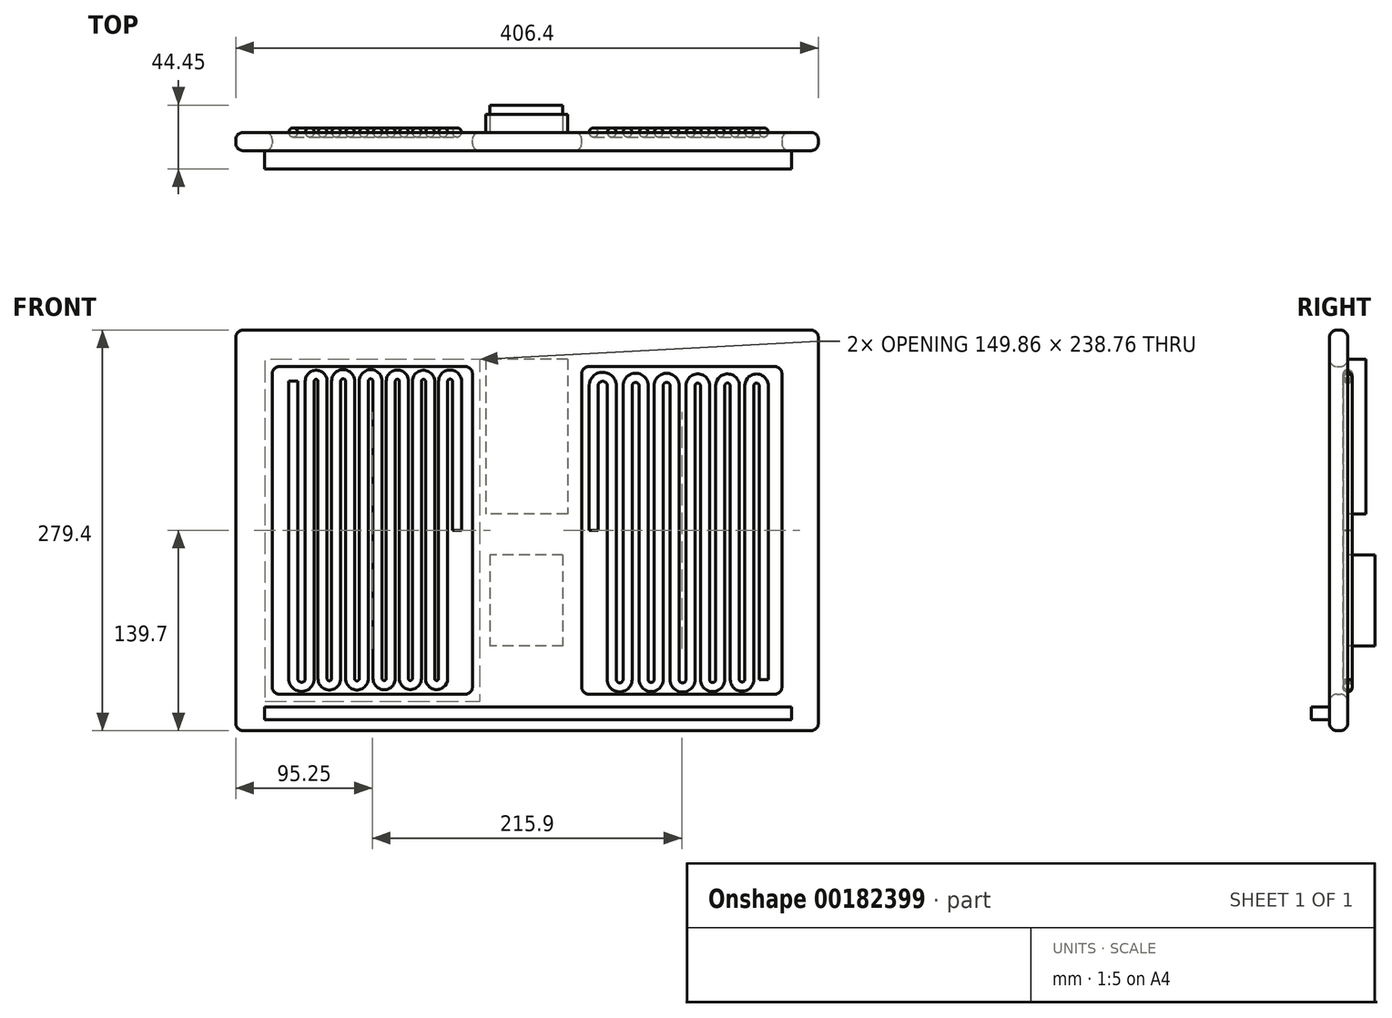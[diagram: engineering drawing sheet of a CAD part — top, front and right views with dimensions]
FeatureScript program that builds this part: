
annotation { "Feature Type Name" : "Feature", "Feature Type Description" : "" }
export const myFeature = defineFeature(function(context is Context, id is Id, definition is map)
    precondition{}
    {
        {
            var Q0;
            Q0=qCreatedBy(makeId("Front.planeOp"),FACE);
            var sketch = newSketch(context, id + "F0", { "sketchPlane" : qUnion([Q0])});
            skLineSegment(sketch, "E0.bottom", {"start": v(-203.2, 139.7) * mm, "end": v(203.2, 139.7) * mm});
            skLineSegment(sketch, "E0.top", {"start": v(-203.2, -139.7) * mm, "end": v(203.2, -139.7) * mm});
            skLineSegment(sketch, "E0.left", {"start": v(-203.2, 139.7) * mm, "end": v(-203.2, -139.7) * mm});
            skLineSegment(sketch, "E0.right", {"start": v(203.2, 139.7) * mm, "end": v(203.2, -139.7) * mm});
            skPoint(sketch, "E0.middle", {"position": v(0, 0) * mm});
            skSolve(sketch);
        }
        {
            var Q0;
            Q0=makeQuery(id+"F0.imprint","IMPRINT",FACE,{"disambiguationData":[TD([[makeQuery(id+"F0.imprint","IMPRINT",EDGE,{"derivedFrom":sQuery(id+"F0.wireOp",EDGE,"E0.bottom")}),-1.0]])]});
            extrude(context, id + "F1", {"entities" : qUnion([Q0]), "depth" : 12.7 * mm});
        }
        {
            var Q0;
            Q0=makeQuery(id+"F1.opExtrude","CAP_FACE",FACE,{"disambiguationData":[OSD([sQuery(id+"F0.wireOp",EDGE,"E0.bottom"),sQuery(id+"F0.wireOp",EDGE,"E0.top"),sQuery(id+"F0.wireOp",EDGE,"E0.left"),sQuery(id+"F0.wireOp",EDGE,"E0.right")])],"isStart":false});
            var sketch = newSketch(context, id + "F2", { "sketchPlane" : qUnion([Q0])});
            skLineSegment(sketch, "E1.bottom", {"start": v(-177.8, 114.3) * mm, "end": v(177.8, 114.3) * mm});
            skLineSegment(sketch, "E1.top", {"start": v(-177.8, -114.3) * mm, "end": v(177.8, -114.3) * mm});
            skLineSegment(sketch, "E1.left", {"start": v(-177.8, 114.3) * mm, "end": v(-177.8, -114.3) * mm});
            skLineSegment(sketch, "E1.right", {"start": v(177.8, 114.3) * mm, "end": v(177.8, -114.3) * mm});
            skPoint(sketch, "E1.middle", {"position": v(0, 0) * mm});
            skSolve(sketch);
        }
        {
            var Q0;
            Q0=makeQuery(id+"F2.imprint","IMPRINT",FACE,{"disambiguationData":[TD([[makeQuery(id+"F2.imprint","IMPRINT",EDGE,{"derivedFrom":sQuery(id+"F2.wireOp",EDGE,"E1.bottom")}),-1.0]])]});
            extrude(context, id + "F3", {"entities" : qUnion([Q0]), "operationType" : NewBodyOperationType.REMOVE, "oppositeDirection" : true, "depth" : 12.7 * mm});
        }
        {
            var Q0;
            Q0=qCreatedBy(makeId("Front.planeOp"),FACE);
            var sketch = newSketch(context, id + "F4", { "sketchPlane" : qUnion([Q0])});
            skLineSegment(sketch, "E2.bottom", {"start": v(-38.1, 114.3) * mm, "end": v(38.1, 114.3) * mm});
            skLineSegment(sketch, "E2.top", {"start": v(-38.1, -114.3) * mm, "end": v(38.1, -114.3) * mm});
            skLineSegment(sketch, "E2.left", {"start": v(-38.1, 114.3) * mm, "end": v(-38.1, -114.3) * mm});
            skLineSegment(sketch, "E2.right", {"start": v(38.1, 114.3) * mm, "end": v(38.1, -114.3) * mm});
            skPoint(sketch, "E2.middle", {"position": v(0, 0) * mm});
            skSolve(sketch);
        }
        {
            var Q0;
            Q0=makeQuery(id+"F4.imprint","IMPRINT",FACE,{"disambiguationData":[TD([[makeQuery(id+"F4.imprint","IMPRINT",EDGE,{"derivedFrom":sQuery(id+"F4.wireOp",EDGE,"E2.bottom")}),-1.0]])]});
            extrude(context, id + "F5", {"entities" : qUnion([Q0]), "operationType" : NewBodyOperationType.ADD, "depth" : 12.7 * mm});
        }
        {
            var Q0;
            Q0=makeQuery(id+"F1.opExtrude","SWEPT_FACE",FACE,{"disambiguationData":[OSD([sQuery(id+"F0.wireOp",EDGE,"E0.bottom")])]});
            var Q1;
            Q1=makeQuery(id+"F1.opExtrude","SWEPT_FACE",FACE,{"disambiguationData":[OSD([sQuery(id+"F0.wireOp",EDGE,"E0.top")])]});
            var Q2;
            Q2=makeQuery(id+"F1.opExtrude","SWEPT_FACE",FACE,{"disambiguationData":[OSD([sQuery(id+"F0.wireOp",EDGE,"E0.left")])]});
            var Q3;
            Q3=makeQuery(id+"F1.opExtrude","CAP_EDGE",EDGE,{"disambiguationData":[OSD([sQuery(id+"F0.wireOp",EDGE,"E0.bottom")])],"isStart":false});
            var Q4;
            Q4=makeQuery(id+"F1.opExtrude","SWEPT_FACE",FACE,{"disambiguationData":[OSD([sQuery(id+"F0.wireOp",EDGE,"E0.right")])]});
            var Q5;
            Q5=makeQuery(id+"F1.opExtrude","CAP_EDGE",EDGE,{"disambiguationData":[OSD([sQuery(id+"F0.wireOp",EDGE,"E0.top")])],"isStart":true});
            var Q6;
            Q6=makeQuery(id+"F1.opExtrude","CAP_EDGE",EDGE,{"disambiguationData":[OSD([sQuery(id+"F0.wireOp",EDGE,"E0.top")])],"isStart":false});
            var Q7;
            Q7=makeQuery(id+"F1.opExtrude","CAP_EDGE",EDGE,{"disambiguationData":[OSD([sQuery(id+"F0.wireOp",EDGE,"E0.left")])],"isStart":false});
            var Q8;
            Q8=makeQuery(id+"F1.opExtrude","CAP_EDGE",EDGE,{"disambiguationData":[OSD([sQuery(id+"F0.wireOp",EDGE,"E0.right")])],"isStart":true});
            var Q9;
            Q9=makeQuery(id+"F1.opExtrude","CAP_EDGE",EDGE,{"disambiguationData":[OSD([sQuery(id+"F0.wireOp",EDGE,"E0.right")])],"isStart":false});
            var Q10;
            Q10=makeQuery(id+"F3.boolean.opBoolean","COPY",FACE,{"derivedFrom":makeQuery(id+"F3.opExtrude","SWEPT_FACE",FACE,{"disambiguationData":[OSD([sQuery(id+"F2.wireOp",EDGE,"E1.left")])]})});
            var Q11;
            Q11=makeQuery(id+"F3.boolean.opBoolean","COPY",FACE,{"derivedFrom":makeQuery(id+"F3.opExtrude","SWEPT_FACE",FACE,{"disambiguationData":[OSD([sQuery(id+"F2.wireOp",EDGE,"E1.right")])]})});
            var Q12;
            Q12=makeQuery(id+"F3.boolean.opBoolean","COPY",EDGE,{"derivedFrom":makeQuery(id+"F3.opExtrude","CAP_EDGE",EDGE,{"disambiguationData":[OSD([sQuery(id+"F2.wireOp",EDGE,"E1.left")])],"isStart":true})});
            var Q13;
            Q13=makeQuery(id+"F3.boolean.opBoolean","COPY",EDGE,{"derivedFrom":makeQuery(id+"F3.opExtrude","CAP_EDGE",EDGE,{"disambiguationData":[OSD([sQuery(id+"F2.wireOp",EDGE,"E1.left")])],"isStart":false})});
            var Q14;
            Q14=makeQuery(id+"F3.boolean.opBoolean","COPY",EDGE,{"derivedFrom":makeQuery(id+"F3.opExtrude","CAP_EDGE",EDGE,{"disambiguationData":[OSD([sQuery(id+"F2.wireOp",EDGE,"E1.right")])],"isStart":true})});
            var Q15;
            Q15=makeQuery(id+"F5.opExtrude","SWEPT_FACE",FACE,{"disambiguationData":[OSD([sQuery(id+"F4.wireOp",EDGE,"E2.left")])]});
            var Q16;
            Q16=makeQuery(id+"F5.opExtrude","SWEPT_FACE",FACE,{"disambiguationData":[OSD([sQuery(id+"F4.wireOp",EDGE,"E2.right")])]});
            var Q17;
            Q17=makeQuery(id+"F5.opExtrude","CAP_EDGE",EDGE,{"disambiguationData":[OSD([sQuery(id+"F4.wireOp",EDGE,"E2.left")])],"isStart":false});
            var Q18;
            Q18=makeQuery(id+"F5.opExtrude","CAP_EDGE",EDGE,{"disambiguationData":[OSD([sQuery(id+"F4.wireOp",EDGE,"E2.right")])],"isStart":true});
            var Q19;
            Q19=makeQuery(id+"F5.opExtrude","CAP_EDGE",EDGE,{"disambiguationData":[OSD([sQuery(id+"F4.wireOp",EDGE,"E2.right")])],"isStart":false});
            var Q20;
            Q20=makeQuery(id+"F5.boolean.opBoolean","MERGE",FACE,{"derivedFrom":[makeQuery(id+"F1.opExtrude","CAP_FACE",FACE,{"disambiguationData":[OSD([sQuery(id+"F0.wireOp",EDGE,"E0.bottom"),sQuery(id+"F0.wireOp",EDGE,"E0.top"),sQuery(id+"F0.wireOp",EDGE,"E0.left"),sQuery(id+"F0.wireOp",EDGE,"E0.right")])],"isStart":true}),makeQuery(id+"F5.opExtrude","CAP_FACE",FACE,{"disambiguationData":[OSD([sQuery(id+"F4.wireOp",EDGE,"E2.bottom"),sQuery(id+"F4.wireOp",EDGE,"E2.top"),sQuery(id+"F4.wireOp",EDGE,"E2.left"),sQuery(id+"F4.wireOp",EDGE,"E2.right")])],"isStart":true})]});
            var Q21;
            Q21=makeQuery(id+"F5.boolean.opBoolean","MERGE",FACE,{"derivedFrom":[makeQuery(id+"F1.opExtrude","CAP_FACE",FACE,{"disambiguationData":[OSD([sQuery(id+"F0.wireOp",EDGE,"E0.bottom"),sQuery(id+"F0.wireOp",EDGE,"E0.top"),sQuery(id+"F0.wireOp",EDGE,"E0.left"),sQuery(id+"F0.wireOp",EDGE,"E0.right")])],"isStart":false}),makeQuery(id+"F5.opExtrude","CAP_FACE",FACE,{"disambiguationData":[OSD([sQuery(id+"F4.wireOp",EDGE,"E2.bottom"),sQuery(id+"F4.wireOp",EDGE,"E2.top"),sQuery(id+"F4.wireOp",EDGE,"E2.left"),sQuery(id+"F4.wireOp",EDGE,"E2.right")])],"isStart":false})]});
            var Q22;
            Q22=makeQuery(id+"F5.boolean.opBoolean","SPLIT",FACE,{"disambiguationData":[TD([makeQuery(id+"F3.boolean.opBoolean","COPY",FACE,{"derivedFrom":makeQuery(id+"F3.opExtrude","SWEPT_FACE",FACE,{"disambiguationData":[OSD([sQuery(id+"F2.wireOp",EDGE,"E1.left")])]})})])],"derivedFrom":makeQuery(id+"F3.boolean.opBoolean","COPY",FACE,{"derivedFrom":makeQuery(id+"F3.opExtrude","SWEPT_FACE",FACE,{"disambiguationData":[OSD([sQuery(id+"F2.wireOp",EDGE,"E1.bottom")])]})})});
            var Q23;
            Q23=makeQuery(id+"F5.boolean.opBoolean","SPLIT",FACE,{"disambiguationData":[TD([makeQuery(id+"F3.boolean.opBoolean","COPY",FACE,{"derivedFrom":makeQuery(id+"F3.opExtrude","SWEPT_FACE",FACE,{"disambiguationData":[OSD([sQuery(id+"F2.wireOp",EDGE,"E1.right")])]})})])],"derivedFrom":makeQuery(id+"F3.boolean.opBoolean","COPY",FACE,{"derivedFrom":makeQuery(id+"F3.opExtrude","SWEPT_FACE",FACE,{"disambiguationData":[OSD([sQuery(id+"F2.wireOp",EDGE,"E1.bottom")])]})})});
            var Q24;
            {var subQ0=sQuery(id+"F2.wireOp",EDGE,"E1.bottom");Q24=makeQuery(id+"F5.boolean.opBoolean","SPLIT",EDGE,{"disambiguationData":[TD([makeQuery(id+"F3.boolean.opBoolean","COPY",FACE,{"derivedFrom":makeQuery(id+"F3.opExtrude","SWEPT_FACE",FACE,{"disambiguationData":[OSD([sQuery(id+"F2.wireOp",EDGE,"E1.left")])]})})])],"derivedFrom":makeQuery(id+"F3.boolean.opBoolean","COPY",EDGE,{"derivedFrom":makeQuery(id+"F3.opExtrude","CAP_EDGE",EDGE,{"disambiguationData":[OSD([subQ0])],"isStart":true})})});}
            var Q25;
            {var subQ1=sQuery(id+"F2.wireOp",EDGE,"E1.bottom");Q25=makeQuery(id+"F5.boolean.opBoolean","SPLIT",EDGE,{"disambiguationData":[TD([makeQuery(id+"F3.boolean.opBoolean","COPY",FACE,{"derivedFrom":makeQuery(id+"F3.opExtrude","SWEPT_FACE",FACE,{"disambiguationData":[OSD([sQuery(id+"F2.wireOp",EDGE,"E1.left")])]})})])],"derivedFrom":makeQuery(id+"F3.boolean.opBoolean","COPY",EDGE,{"derivedFrom":makeQuery(id+"F3.opExtrude","CAP_EDGE",EDGE,{"disambiguationData":[OSD([subQ1])],"isStart":false})})});}
            var Q26;
            {var subQ1=sQuery(id+"F2.wireOp",EDGE,"E1.bottom");Q26=makeQuery(id+"F5.boolean.opBoolean","SPLIT",EDGE,{"disambiguationData":[TD([makeQuery(id+"F3.boolean.opBoolean","COPY",FACE,{"derivedFrom":makeQuery(id+"F3.opExtrude","SWEPT_FACE",FACE,{"disambiguationData":[OSD([sQuery(id+"F2.wireOp",EDGE,"E1.right")])]})})])],"derivedFrom":makeQuery(id+"F3.boolean.opBoolean","COPY",EDGE,{"derivedFrom":makeQuery(id+"F3.opExtrude","CAP_EDGE",EDGE,{"disambiguationData":[OSD([subQ1])],"isStart":false})})});}
            var Q27;
            {var subQ0=sQuery(id+"F2.wireOp",EDGE,"E1.top");Q27=makeQuery(id+"F5.boolean.opBoolean","SPLIT",EDGE,{"disambiguationData":[TD([makeQuery(id+"F3.boolean.opBoolean","COPY",FACE,{"derivedFrom":makeQuery(id+"F3.opExtrude","SWEPT_FACE",FACE,{"disambiguationData":[OSD([sQuery(id+"F2.wireOp",EDGE,"E1.left")])]})})])],"derivedFrom":makeQuery(id+"F3.boolean.opBoolean","COPY",EDGE,{"derivedFrom":makeQuery(id+"F3.opExtrude","CAP_EDGE",EDGE,{"disambiguationData":[OSD([subQ0])],"isStart":true})})});}
            var Q28;
            Q28=makeQuery(id+"F1.opExtrude","SWEPT_EDGE",EDGE,{"disambiguationData":[OSD([sQuery(id+"F0.wireOp",EDGE,"E0.bottom"),sQuery(id+"F0.wireOp",EDGE,"E0.left")])]});
            var Q29;
            Q29=makeQuery(id+"F1.opExtrude","SWEPT_EDGE",EDGE,{"disambiguationData":[OSD([sQuery(id+"F0.wireOp",EDGE,"E0.bottom"),sQuery(id+"F0.wireOp",EDGE,"E0.right")])]});
            var Q30;
            Q30=makeQuery(id+"F1.opExtrude","SWEPT_EDGE",EDGE,{"disambiguationData":[OSD([sQuery(id+"F0.wireOp",EDGE,"E0.top"),sQuery(id+"F0.wireOp",EDGE,"E0.left")])]});
            var Q31;
            Q31=makeQuery(id+"F1.opExtrude","SWEPT_EDGE",EDGE,{"disambiguationData":[OSD([sQuery(id+"F0.wireOp",EDGE,"E0.top"),sQuery(id+"F0.wireOp",EDGE,"E0.right")])]});
            var Q32;
            Q32=makeQuery(id+"F1.opExtrude","CAP_EDGE",EDGE,{"disambiguationData":[OSD([sQuery(id+"F0.wireOp",EDGE,"E0.bottom")])],"isStart":true});
            var Q33;
            Q33=makeQuery(id+"F1.opExtrude","CAP_EDGE",EDGE,{"disambiguationData":[OSD([sQuery(id+"F0.wireOp",EDGE,"E0.left")])],"isStart":true});
            var Q34;
            Q34=makeQuery(id+"F3.boolean.opBoolean","COPY",EDGE,{"derivedFrom":makeQuery(id+"F3.opExtrude","SWEPT_EDGE",EDGE,{"disambiguationData":[OSD([sQuery(id+"F2.wireOp",EDGE,"E1.bottom"),sQuery(id+"F2.wireOp",EDGE,"E1.left")])]})});
            var Q35;
            Q35=makeQuery(id+"F3.boolean.opBoolean","COPY",EDGE,{"derivedFrom":makeQuery(id+"F3.opExtrude","SWEPT_EDGE",EDGE,{"disambiguationData":[OSD([sQuery(id+"F2.wireOp",EDGE,"E1.bottom"),sQuery(id+"F2.wireOp",EDGE,"E1.right")])]})});
            var Q36;
            Q36=makeQuery(id+"F3.boolean.opBoolean","COPY",EDGE,{"derivedFrom":makeQuery(id+"F3.opExtrude","CAP_EDGE",EDGE,{"disambiguationData":[OSD([sQuery(id+"F2.wireOp",EDGE,"E1.right")])],"isStart":false})});
            var Q37;
            Q37=makeQuery(id+"F5.opExtrude","CAP_EDGE",EDGE,{"disambiguationData":[OSD([sQuery(id+"F4.wireOp",EDGE,"E2.left")])],"isStart":true});
            var Q38;
            Q38=makeQuery(id+"F5.opExtrude","SWEPT_EDGE",EDGE,{"disambiguationData":[OSD([sQuery(id+"F4.wireOp",EDGE,"E2.bottom"),sQuery(id+"F4.wireOp",EDGE,"E2.left")])]});
            var Q39;
            Q39=makeQuery(id+"F5.opExtrude","SWEPT_EDGE",EDGE,{"disambiguationData":[OSD([sQuery(id+"F4.wireOp",EDGE,"E2.bottom"),sQuery(id+"F4.wireOp",EDGE,"E2.right")])]});
            var Q40;
            Q40=makeQuery(id+"F5.opExtrude","SWEPT_EDGE",EDGE,{"disambiguationData":[OSD([sQuery(id+"F4.wireOp",EDGE,"E2.top"),sQuery(id+"F4.wireOp",EDGE,"E2.left")])]});
            var Q41;
            Q41=makeQuery(id+"F5.opExtrude","SWEPT_EDGE",EDGE,{"disambiguationData":[OSD([sQuery(id+"F4.wireOp",EDGE,"E2.top"),sQuery(id+"F4.wireOp",EDGE,"E2.right")])]});
            var Q42;
            Q42=makeQuery(id+"F5.boolean.opBoolean","SPLIT",FACE,{"disambiguationData":[TD([makeQuery(id+"F3.boolean.opBoolean","COPY",FACE,{"derivedFrom":makeQuery(id+"F3.opExtrude","SWEPT_FACE",FACE,{"disambiguationData":[OSD([sQuery(id+"F2.wireOp",EDGE,"E1.left")])]})})])],"derivedFrom":makeQuery(id+"F3.boolean.opBoolean","COPY",FACE,{"derivedFrom":makeQuery(id+"F3.opExtrude","SWEPT_FACE",FACE,{"disambiguationData":[OSD([sQuery(id+"F2.wireOp",EDGE,"E1.top")])]})})});
            var Q43;
            {var subQ0=sQuery(id+"F2.wireOp",EDGE,"E1.bottom");Q43=makeQuery(id+"F5.boolean.opBoolean","SPLIT",EDGE,{"disambiguationData":[TD([makeQuery(id+"F3.boolean.opBoolean","COPY",FACE,{"derivedFrom":makeQuery(id+"F3.opExtrude","SWEPT_FACE",FACE,{"disambiguationData":[OSD([sQuery(id+"F2.wireOp",EDGE,"E1.right")])]})})])],"derivedFrom":makeQuery(id+"F3.boolean.opBoolean","COPY",EDGE,{"derivedFrom":makeQuery(id+"F3.opExtrude","CAP_EDGE",EDGE,{"disambiguationData":[OSD([subQ0])],"isStart":true})})});}
            var Q44;
            Q44=makeQuery(id+"F5.boolean.opBoolean","SPLIT",FACE,{"disambiguationData":[TD([makeQuery(id+"F3.boolean.opBoolean","COPY",FACE,{"derivedFrom":makeQuery(id+"F3.opExtrude","SWEPT_FACE",FACE,{"disambiguationData":[OSD([sQuery(id+"F2.wireOp",EDGE,"E1.right")])]})})])],"derivedFrom":makeQuery(id+"F3.boolean.opBoolean","COPY",FACE,{"derivedFrom":makeQuery(id+"F3.opExtrude","SWEPT_FACE",FACE,{"disambiguationData":[OSD([sQuery(id+"F2.wireOp",EDGE,"E1.top")])]})})});
            var Q45;
            {var subQ0=sQuery(id+"F2.wireOp",EDGE,"E1.top");Q45=makeQuery(id+"F5.boolean.opBoolean","SPLIT",EDGE,{"disambiguationData":[TD([makeQuery(id+"F3.boolean.opBoolean","COPY",FACE,{"derivedFrom":makeQuery(id+"F3.opExtrude","SWEPT_FACE",FACE,{"disambiguationData":[OSD([sQuery(id+"F2.wireOp",EDGE,"E1.right")])]})})])],"derivedFrom":makeQuery(id+"F3.boolean.opBoolean","COPY",EDGE,{"derivedFrom":makeQuery(id+"F3.opExtrude","CAP_EDGE",EDGE,{"disambiguationData":[OSD([subQ0])],"isStart":true})})});}
            var Q46;
            {var subQ1=sQuery(id+"F2.wireOp",EDGE,"E1.top");Q46=makeQuery(id+"F5.boolean.opBoolean","SPLIT",EDGE,{"disambiguationData":[TD([makeQuery(id+"F3.boolean.opBoolean","COPY",FACE,{"derivedFrom":makeQuery(id+"F3.opExtrude","SWEPT_FACE",FACE,{"disambiguationData":[OSD([sQuery(id+"F2.wireOp",EDGE,"E1.right")])]})})])],"derivedFrom":makeQuery(id+"F3.boolean.opBoolean","COPY",EDGE,{"derivedFrom":makeQuery(id+"F3.opExtrude","CAP_EDGE",EDGE,{"disambiguationData":[OSD([subQ1])],"isStart":false})})});}
            var Q47;
            Q47=makeQuery(id+"F3.boolean.opBoolean","COPY",EDGE,{"derivedFrom":makeQuery(id+"F3.opExtrude","SWEPT_EDGE",EDGE,{"disambiguationData":[OSD([sQuery(id+"F2.wireOp",EDGE,"E1.top"),sQuery(id+"F2.wireOp",EDGE,"E1.left")])]})});
            var Q48;
            Q48=makeQuery(id+"F3.boolean.opBoolean","COPY",EDGE,{"derivedFrom":makeQuery(id+"F3.opExtrude","SWEPT_EDGE",EDGE,{"disambiguationData":[OSD([sQuery(id+"F2.wireOp",EDGE,"E1.top"),sQuery(id+"F2.wireOp",EDGE,"E1.right")])]})});
            var Q49;
            {var subQ1=sQuery(id+"F2.wireOp",EDGE,"E1.top");Q49=makeQuery(id+"F5.boolean.opBoolean","SPLIT",EDGE,{"disambiguationData":[TD([makeQuery(id+"F3.boolean.opBoolean","COPY",FACE,{"derivedFrom":makeQuery(id+"F3.opExtrude","SWEPT_FACE",FACE,{"disambiguationData":[OSD([sQuery(id+"F2.wireOp",EDGE,"E1.left")])]})})])],"derivedFrom":makeQuery(id+"F3.boolean.opBoolean","COPY",EDGE,{"derivedFrom":makeQuery(id+"F3.opExtrude","CAP_EDGE",EDGE,{"disambiguationData":[OSD([subQ1])],"isStart":false})})});}
            fillet(context, id + "F6", {"entities" : qUnion([Q0, Q1, Q2, Q3, Q4, Q5, Q6, Q7, Q8, Q9, Q10, Q11, Q12, Q13, Q14, Q15, Q16, Q17, Q18, Q19, Q20, Q21, Q22, Q23, Q24, Q25, Q26, Q27, Q28, Q29, Q30, Q31, Q32, Q33, Q34, Q35, Q36, Q37, Q38, Q39, Q40, Q41, Q42, Q43, Q44, Q45, Q46, Q47, Q48, Q49]), "radius" : 5.08 * mm, "tangentPropagation" : true, "allowEdgeOverflow" : false});
        }
        {
            var Q0;
            Q0=qCreatedBy(makeId("Front.planeOp"),FACE);
            var sketch = newSketch(context, id + "F7", { "sketchPlane" : qUnion([Q0])});
            skLineSegment(sketch, "E3", {"start": v(46.45, 0) * mm, "end": v(46.45, 100.84) * mm});
            skArc(sketch, "E4", {"start": v(46.45, 100.84) * mm, "mid": v(52.76, 107.15) * mm, "end": v(59.07, 100.84) * mm});
            skLineSegment(sketch, "E5", {"start": v(59.07, 100.84) * mm, "end": v(59.07, -104.04) * mm});
            skArc(sketch, "E6", {"start": v(59.07, -104.04) * mm, "mid": v(64.58, -109.56) * mm, "end": v(70.1, -104.04) * mm});
            skLineSegment(sketch, "E7", {"start": v(70.1, -104.04) * mm, "end": v(70.1, 100.84) * mm});
            skArc(sketch, "E8", {"start": v(70.1, 100.84) * mm, "mid": v(75.7, 106.45) * mm, "end": v(81.3, 100.84) * mm});
            skLineSegment(sketch, "E9", {"start": v(81.3, 100.84) * mm, "end": v(81.3, -104.04) * mm});
            skArc(sketch, "E10", {"start": v(81.3, -104.04) * mm, "mid": v(86.57, -109.3) * mm, "end": v(91.83, -104.04) * mm});
            skLineSegment(sketch, "E11", {"start": v(91.83, -104.04) * mm, "end": v(91.83, 100.84) * mm});
            skArc(sketch, "E12", {"start": v(91.83, 100.84) * mm, "mid": v(97.37, 106.38) * mm, "end": v(102.92, 100.84) * mm});
            skLineSegment(sketch, "E13", {"start": v(102.92, 100.84) * mm, "end": v(102.92, -104.04) * mm});
            skArc(sketch, "E14", {"start": v(102.92, -104.04) * mm, "mid": v(108.46, -109.59) * mm, "end": v(114, -104.04) * mm});
            skLineSegment(sketch, "E15", {"start": v(114, -104.04) * mm, "end": v(114, 100.84) * mm});
            skArc(sketch, "E16", {"start": v(114, 100.84) * mm, "mid": v(119.07, 105.9) * mm, "end": v(124.13, 100.84) * mm});
            skLineSegment(sketch, "E17", {"start": v(124.13, 100.84) * mm, "end": v(124.13, -104.04) * mm});
            skArc(sketch, "E18", {"start": v(124.13, -104.04) * mm, "mid": v(129.43, -109.35) * mm, "end": v(134.73, -104.04) * mm});
            skLineSegment(sketch, "E19", {"start": v(134.73, -104.04) * mm, "end": v(134.73, 100.84) * mm});
            skArc(sketch, "E20", {"start": v(134.73, 100.84) * mm, "mid": v(139.84, 105.95) * mm, "end": v(144.95, 100.84) * mm});
            skLineSegment(sketch, "E21", {"start": v(144.95, 100.84) * mm, "end": v(144.95, -104.04) * mm});
            skArc(sketch, "E22", {"start": v(144.95, -104.04) * mm, "mid": v(149.96, -109.06) * mm, "end": v(154.98, -104.04) * mm});
            skLineSegment(sketch, "E23", {"start": v(154.98, -104.04) * mm, "end": v(154.98, 100.84) * mm});
            skArc(sketch, "E24", {"start": v(154.98, 100.84) * mm, "mid": v(160.04, 105.9) * mm, "end": v(165.1, 100.84) * mm});
            skLineSegment(sketch, "E25", {"start": v(165.1, 100.84) * mm, "end": v(165.1, -104.04) * mm});
            skSolve(sketch);
        }
        {
            var Q0;
            Q0=qCreatedBy(makeId("Top.planeOp"),FACE);
            var sketch = newSketch(context, id + "F8", { "sketchPlane" : qUnion([Q0])});
            skCircle(sketch, "E26", {"center": v(46.45, 0) * mm, "radius": 3.17 * mm});
            skSolve(sketch);
        }
        {
            var Q0;
            Q0=makeQuery(id+"F8.imprint","IMPRINT",FACE,{"disambiguationData":[TD([[makeQuery(id+"F8.imprint","IMPRINT",EDGE,{"derivedFrom":sQuery(id+"F8.wireOp",EDGE,"E26")}),1.0]])]});
            var Q1;
            Q1 = qConstructionFilter(qBodyType(qCreatedBy(id + "F7" ,EDGE), BodyType.WIRE), ConstructionObject.NO);
            sweep(context, id + "F9", {"profiles" : qUnion([Q0]), "path" : qUnion([Q1])});
        }
        {
            var Q0;
            Q0=qCreatedBy(makeId("Front.planeOp"),FACE);
            var sketch = newSketch(context, id + "F10", { "sketchPlane" : qUnion([Q0])});
            skLineSegment(sketch, "E27", {"start": v(-48.91, 0) * mm, "end": v(-48.91, 103.93) * mm});
            skArc(sketch, "E28", {"start": v(-48.91, 103.93) * mm, "mid": v(-53.73, 108.75) * mm, "end": v(-58.55, 103.93) * mm});
            skLineSegment(sketch, "E29", {"start": v(-58.55, 103.93) * mm, "end": v(-58.55, -103.38) * mm});
            skArc(sketch, "E30", {"start": v(-58.55, -103.38) * mm, "mid": v(-63.1, -107.93) * mm, "end": v(-67.65, -103.38) * mm});
            skLineSegment(sketch, "E31", {"start": v(-67.65, -103.38) * mm, "end": v(-67.65, 103.93) * mm});
            skArc(sketch, "E32", {"start": v(-67.65, 103.93) * mm, "mid": v(-72.27, 108.55) * mm, "end": v(-76.88, 103.93) * mm});
            skLineSegment(sketch, "E33", {"start": v(-76.88, 103.93) * mm, "end": v(-76.88, -103.38) * mm});
            skArc(sketch, "E34", {"start": v(-76.88, -103.38) * mm, "mid": v(-81.4, -107.9) * mm, "end": v(-85.93, -103.38) * mm});
            skLineSegment(sketch, "E35", {"start": v(-85.93, -103.38) * mm, "end": v(-85.93, 104.11) * mm});
            skArc(sketch, "E36", {"start": v(-85.93, 104.11) * mm, "mid": v(-90.5, 108.68) * mm, "end": v(-95.07, 104.11) * mm});
            skLineSegment(sketch, "E37", {"start": v(-95.07, 104.11) * mm, "end": v(-95.07, -103.38) * mm});
            skArc(sketch, "E38", {"start": v(-95.07, -103.38) * mm, "mid": v(-99.68, -107.99) * mm, "end": v(-104.28, -103.38) * mm});
            skLineSegment(sketch, "E39", {"start": v(-104.28, -103.38) * mm, "end": v(-104.28, 104.11) * mm});
            skArc(sketch, "E40", {"start": v(-104.28, 104.11) * mm, "mid": v(-109.1, 108.92) * mm, "end": v(-113.9, 104.11) * mm});
            skLineSegment(sketch, "E41", {"start": v(-113.9, 104.11) * mm, "end": v(-113.9, -103.38) * mm});
            skArc(sketch, "E42", {"start": v(-113.9, -103.38) * mm, "mid": v(-118.67, -108.16) * mm, "end": v(-123.45, -103.38) * mm});
            skLineSegment(sketch, "E43", {"start": v(-123.45, -103.38) * mm, "end": v(-123.45, 104.11) * mm});
            skArc(sketch, "E44", {"start": v(-123.45, 104.11) * mm, "mid": v(-128.31, 108.97) * mm, "end": v(-133.17, 104.11) * mm});
            skLineSegment(sketch, "E45", {"start": v(-133.17, 104.11) * mm, "end": v(-133.17, -103.38) * mm});
            skArc(sketch, "E46", {"start": v(-133.17, -103.38) * mm, "mid": v(-137.93, -108.14) * mm, "end": v(-142.7, -103.38) * mm});
            skLineSegment(sketch, "E47", {"start": v(-142.7, -103.38) * mm, "end": v(-142.7, 104.11) * mm});
            skArc(sketch, "E48", {"start": v(-142.7, 104.11) * mm, "mid": v(-147.13, 108.55) * mm, "end": v(-151.58, 104.11) * mm});
            skLineSegment(sketch, "E49", {"start": v(-151.58, 104.11) * mm, "end": v(-151.58, -103.38) * mm});
            skArc(sketch, "E50", {"start": v(-151.58, -103.38) * mm, "mid": v(-157.34, -109.15) * mm, "end": v(-163.1, -103.38) * mm});
            skLineSegment(sketch, "E51", {"start": v(-163.1, -103.38) * mm, "end": v(-163.1, 104.11) * mm});
            skSolve(sketch);
        }
        {
            var Q0;
            Q0=qCreatedBy(makeId("Top.planeOp"),FACE);
            var sketch = newSketch(context, id + "F11", { "sketchPlane" : qUnion([Q0])});
            skCircle(sketch, "E52", {"center": v(-48.91, 0) * mm, "radius": 3.18 * mm});
            skSolve(sketch);
        }
        {
            var Q0;
            Q0=makeQuery(id+"F11.imprint","IMPRINT",FACE,{"disambiguationData":[TD([[makeQuery(id+"F11.imprint","IMPRINT",EDGE,{"derivedFrom":sQuery(id+"F11.wireOp",EDGE,"E52")}),1.0]])]});
            var Q1;
            Q1 = qConstructionFilter(qBodyType(qCreatedBy(id + "F10" ,EDGE), BodyType.WIRE), ConstructionObject.NO);
            sweep(context, id + "F12", {"profiles" : qUnion([Q0]), "path" : qUnion([Q1])});
        }
        {
            var Q0;
            Q0=qCreatedBy(makeId("Front.planeOp"),FACE);
            var sketch = newSketch(context, id + "F13", { "sketchPlane" : qUnion([Q0])});
            skLineSegment(sketch, "E53.bottom", {"start": v(-183.01, -123.2) * mm, "end": v(184.65, -123.2) * mm});
            skLineSegment(sketch, "E53.top", {"start": v(-183.01, -131.93) * mm, "end": v(184.65, -131.93) * mm});
            skLineSegment(sketch, "E53.left", {"start": v(-183.01, -123.2) * mm, "end": v(-183.01, -131.93) * mm});
            skLineSegment(sketch, "E53.right", {"start": v(184.65, -123.2) * mm, "end": v(184.65, -131.93) * mm});
            skSolve(sketch);
        }
        {
            var Q0;
            Q0 = qSketchRegion(id + "F13", true);
            extrude(context, id + "F14", {"entities" : qUnion([Q0]), "operationType" : NewBodyOperationType.ADD, "depth" : 25.4 * mm});
        }
        {
            var Q0;
            Q0=qCreatedBy(makeId("Front.planeOp"),FACE);
            var sketch = newSketch(context, id + "F15", { "sketchPlane" : qUnion([Q0])});
            skLineSegment(sketch, "E54.bottom", {"start": v(28.28, 119.51) * mm, "end": v(-28.87, 119.51) * mm});
            skLineSegment(sketch, "E54.top", {"start": v(28.28, 11.56) * mm, "end": v(-28.87, 11.56) * mm});
            skLineSegment(sketch, "E54.left", {"start": v(28.28, 119.51) * mm, "end": v(28.28, 11.56) * mm});
            skLineSegment(sketch, "E54.right", {"start": v(-28.87, 119.51) * mm, "end": v(-28.87, 11.56) * mm});
            skSolve(sketch);
        }
        {
            var Q0;
            Q0 = qSketchRegion(id + "F15", true);
            extrude(context, id + "F16", {"entities" : qUnion([Q0]), "oppositeDirection" : true, "depth" : 12.7 * mm});
        }
        {
            var Q0;
            Q0=qCreatedBy(makeId("Front.planeOp"),FACE);
            var sketch = newSketch(context, id + "F17", { "sketchPlane" : qUnion([Q0])});
            skLineSegment(sketch, "E55.bottom", {"start": v(24.9, -17) * mm, "end": v(-25.9, -17) * mm});
            skLineSegment(sketch, "E55.top", {"start": v(24.9, -80.5) * mm, "end": v(-25.9, -80.5) * mm});
            skLineSegment(sketch, "E55.left", {"start": v(24.9, -17) * mm, "end": v(24.9, -80.5) * mm});
            skLineSegment(sketch, "E55.right", {"start": v(-25.9, -17) * mm, "end": v(-25.9, -80.5) * mm});
            skSolve(sketch);
        }
        {
            var Q0;
            Q0 = qSketchRegion(id + "F17", true);
            extrude(context, id + "F18", {"entities" : qUnion([Q0]), "oppositeDirection" : true, "depth" : 19.05 * mm});
        }
    });
